# Revit family: Access_Panel-Wall_Door-Activar-Exterior_Access-XPA
name_source: partatom
category: Doors
revit_build: Autodesk Revit MEP 2012 (Build: 20110309_2315(x64)
units: mm (PartAtom-declared; Revit-internal decimal feet)

## types (16) — shared parameters
04 CSI = 08 31 16
95 CSI = 08310
Additional Info URL = http://www.activarcpg.com
Assembly Code = C1020700
Color Availability = Red (R), Black (BK), Flat Black (FB), Sand (S), AMS Beige (AB), SC Flat Beige (SB), Gray (G), Bronze (B), Silver (SI)
Custom Size Note = Custom sizes are available.  Contact manufacturer for availability.
Default Elevation = 48"
Description = Weather-Resistant Flush Access Panel
Door = 2" Thick Insulated .040 Aluminum Door with Continuous Stainless Steel Hinges and EPDM Foam Rubber Bulb Seal Gasketing.
Frame = 16 Gauge Galvanized Steel Frame with 1" Flange.
Gasket = EPDM Rubber Bulb Gasket
Hardware = Non-locking (H) Die Cast Zinc Handles for Exterior, Interior has Non-locking handle.
Installation URL = http://www.activarcpg.com
Maitenance URL = http://www.activarcpg.com
Manufacturer = Activar Construction Products Group
Manufacturer Fax = 952-835-2218
Options = Optional Colors, Chrome-Plated Locking Handle (H3).
Panel Type Use = Weather-resistant Flush Access Panel for Walls or Ceilings
Product Line = Exterior Access Panels
Product Page URL = http://www.activarcpg.com
Subcategory = Access Panels
Submittal URL = http://www.activarcpg.com
URL = http://www.activarcpg.com
Warranty URL = http://www.activarcpg.com
ecoScorecard Product Page = http://ecoscorecard.com

## per-type parameters (varying)
| type | Height | Model | Number of Latches | Rough Height | Rough Width | Shipping Weight | Width |
| 12 x 12 | 14" | XPA-1212 | 1 | 12 3/8" | 12 3/8" | 11.00 lb | 14" |
| 14 x 14 | 16" | XPA-1414 | 1 | 14 3/8" | 14 3/8" | 15.00 lb | 16" |
| 18 x 18 | 20" | XPA-1818 | 1 | 18 3/8" | 18 3/8" | 19.00 lb | 20" |
| 20 x 24 | 26" | XPA-2024 | 1 | 24 3/8" | 20 3/8" | 30.00 lb | 22" |
| 20 x 30 | 32" | XPA-2030 | 1 | 30 3/8" | 20 3/8" | 32.00 lb | 22" |
| 22 x 30 | 32" | XPA-2230 | 1 | 30 3/8" | 22 3/8" | 34.00 lb | 24" |
| 22 x 36 | 38" | XPA-2236 | 2 | 36 3/8" | 22 3/8" | 40.00 lb | 24" |
| 24 x 24 | 26" | XPA-2424 | 2 | 24 3/8" | 24 3/8" | 27.00 lb | 26" |
| 24 x 30 | 32" | XPA-2430 | 2 | 30 3/8" | 24 3/8" | 40.00 lb | 26" |
| 24 x 36 | 38" | XPA-2436 | 2 | 36 3/8" | 24 3/8" | 42.00 lb | 26" |
| 24 x 48 | 50" | XPA-2448 | 2 | 48 3/8" | 24 3/8" | 57.00 lb | 26" |
| 30 x 30 | 32" | XPA-3030 | 2 | 30 3/8" | 30 3/8" | 44.00 lb | 32" |
| 30 x 36 | 38" | XPA-3036 | 2 | 36 3/8" | 30 3/8" | 56.00 lb | 32" |
| 36 x 36 | 38" | XPA-3636 | 2 | 36 3/8" | 36 3/8" | 61.00 lb | 38" |
| 36 x 48 | 50" | XPA-3648 | 2 | 48 3/8" | 36 3/8" | 75.00 lb | 38" |
| 48 x 48 | 50" | XPA-4848 | 4 | 48 3/8" | 48 3/8" | 108.00 lb | 50" |

## geometry (parser evidence)
native form markers: Sweep x1
no freeform markers — native parametric forms only
